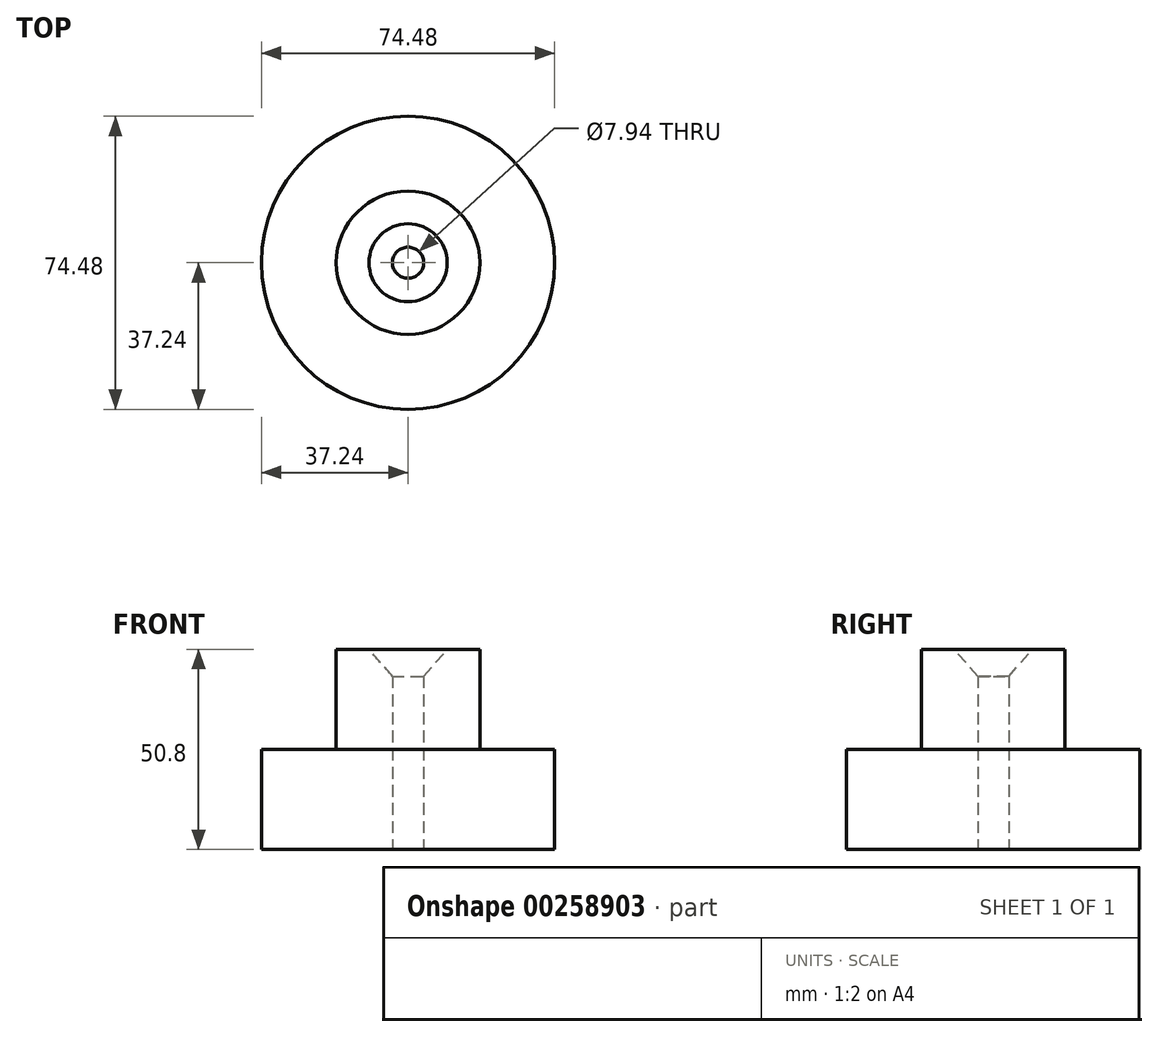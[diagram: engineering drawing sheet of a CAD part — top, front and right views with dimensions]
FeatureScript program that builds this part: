
annotation { "Feature Type Name" : "Feature", "Feature Type Description" : "" }
export const myFeature = defineFeature(function(context is Context, id is Id, definition is map)
    precondition{}
    {
        {
            var Q0;
            Q0=qCreatedBy(makeId("Top.planeOp"),FACE);
            var sketch = newSketch(context, id + "F0", { "sketchPlane" : qUnion([Q0])});
            skCircle(sketch, "E0", {"center": v(0, 0) * mm, "radius": 37.24 * mm});
            skSolve(sketch);
        }
        {
            var Q0;
            Q0 = qSketchRegion(id + "F0", true);
            extrude(context, id + "F1", {"entities" : qUnion([Q0]), "depth" : 25.4 * mm});
        }
        {
            var Q0;
            Q0=makeQuery(id+"F1.opExtrude","CAP_FACE",FACE,{"disambiguationData":[OSD([sQuery(id+"F0.wireOp",EDGE,"E0")])],"isStart":false});
            var sketch = newSketch(context, id + "F2", { "sketchPlane" : qUnion([Q0])});
            skCircle(sketch, "E1", {"center": v(0, 0) * mm, "radius": 18.22 * mm});
            skSolve(sketch);
        }
        {
            var Q0;
            Q0=makeQuery(id+"F2.imprint","IMPRINT",FACE,{"disambiguationData":[TD([[makeQuery(id+"F2.imprint","IMPRINT",EDGE,{"derivedFrom":sQuery(id+"F2.wireOp",EDGE,"E1")}),1.0]])]});
            extrude(context, id + "F3", {"entities" : qUnion([Q0]), "operationType" : NewBodyOperationType.ADD, "depth" : 25.4 * mm});
        }
        {
            var Q0;
            Q0=makeQuery(id+"F3.opExtrude","CAP_FACE",FACE,{"disambiguationData":[OSD([sQuery(id+"F2.wireOp",EDGE,"E1")])],"isStart":false});
            var sketch = newSketch(context, id + "F4", { "sketchPlane" : qUnion([Q0])});
            skPoint(sketch, "E2", {"position": v(0, 0) * mm});
            skSolve(sketch);
        }
        {
            var Q0;
            Q0=sQuery(id+"F4.wireOp",VERTEX,"E2");
            var Q1;
            Q1=makeQuery(id+"F1.opExtrude","SWEPT_BODY",BODY,{"disambiguationData":[OSD([sQuery(id+"F0.wireOp",EDGE,"E0")])]});
            hole(context, id + "F5", {"style" : HoleStyle.C_SINK, "endStyle" : HoleEndStyle.THROUGH, "standardTappedOrClearance" : lookupTablePath({ "standard" : "ANSI", "engagement" : "75%", "pitch" : "16 tpi", "size" : "3/8", "type" : "Tapped" }), "standardBlindInLast" : lookupTablePath({ "standard" : "ANSI", "engagement" : "75%", "pitch" : "16 tpi", "size" : "3/8", "type" : "Tapped" }), "holeDiameter" : 7.94 * mm, "cSinkDiameter" : 19.84 * mm, "cSinkAngle" : 82 * degree, "showTappedDepth" : true, "isTappedThrough" : true, "tappedDepth" : 7.95 * mm, "tapClearance" : 3, "locations" : qUnion([Q0]), "scope" : qUnion([Q1]), "majorDiameter" : 9.53 * mm, "startStyle" : HoleStartStyle.PART});
        }
    });
